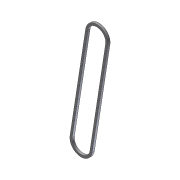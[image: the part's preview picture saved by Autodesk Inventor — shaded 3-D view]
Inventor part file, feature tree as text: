
AUTODESK INVENTOR PART (.ipt)
format: ipt  version: 2012 (Build 160160000, 160)  size: 80,896 bytes
history: native  units: in
note: dims shown in document units (in); Inventor stores cm internally (conversion verified against a paired STEP export)
features: extrude x1, sketch x1
ambient origin geometry x8: Origin, YZ Plane, XZ Plane, XY Plane, X Axis, Y Axis, Z Axis, Center Point
bodies: Solid1 (feature_tree)
feature tree (2):
  extrude  "Extrusion1"  Depth=0.1875in
  sketch  "Sketch1"  dims[d0=8.5in d1=0.1875in d2=0.75in d3=0.1875in d4=0.0in]
